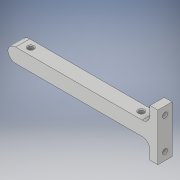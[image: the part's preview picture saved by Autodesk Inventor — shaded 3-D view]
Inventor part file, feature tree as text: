
AUTODESK INVENTOR PART (.ipt)
format: ipt  version: 2019 (Build 230136000, 136)  size: 182,272 bytes
history: native  units: mm
features: fillet x4, extrude x2, sketch x2
ambient origin geometry x8: Origin, YZ Plane, XZ Plane, XY Plane, X Axis, Y Axis, Z Axis, Center Point
bodies: Solid1 (feature_tree)
feature tree (8):
  extrude  "Extrusion1"  Depth=90.0mm
  extrude  "Extrusion2"  Depth=0.5mm
  fillet  "Fillet1"  Radius=3.2mm
  fillet  "Fillet2"  Radius=3.2mm
  fillet  "Fillet3"  Radius=90.0mm
  fillet  "Fillet4"  Radius=9.0mm
  sketch  "Sketch1"  dims[d0=70.0mm d1=90.0mm]
  sketch  "Sketch2"  dims[d2=3.2mm d3=3.2mm d4=3.2mm d5=3.2mm d6=90.0mm d7=9.0mm d8=9.0mm d9=0.0mm d10=9.0mm d11=30.0mm d12=10.0mm d13=10.0mm d14=3.2mm d15=3.2mm d16=5.0mm d17=0.0mm d18=5.0mm d19=5.0mm d20=1.0mm d21=0.5mm]
